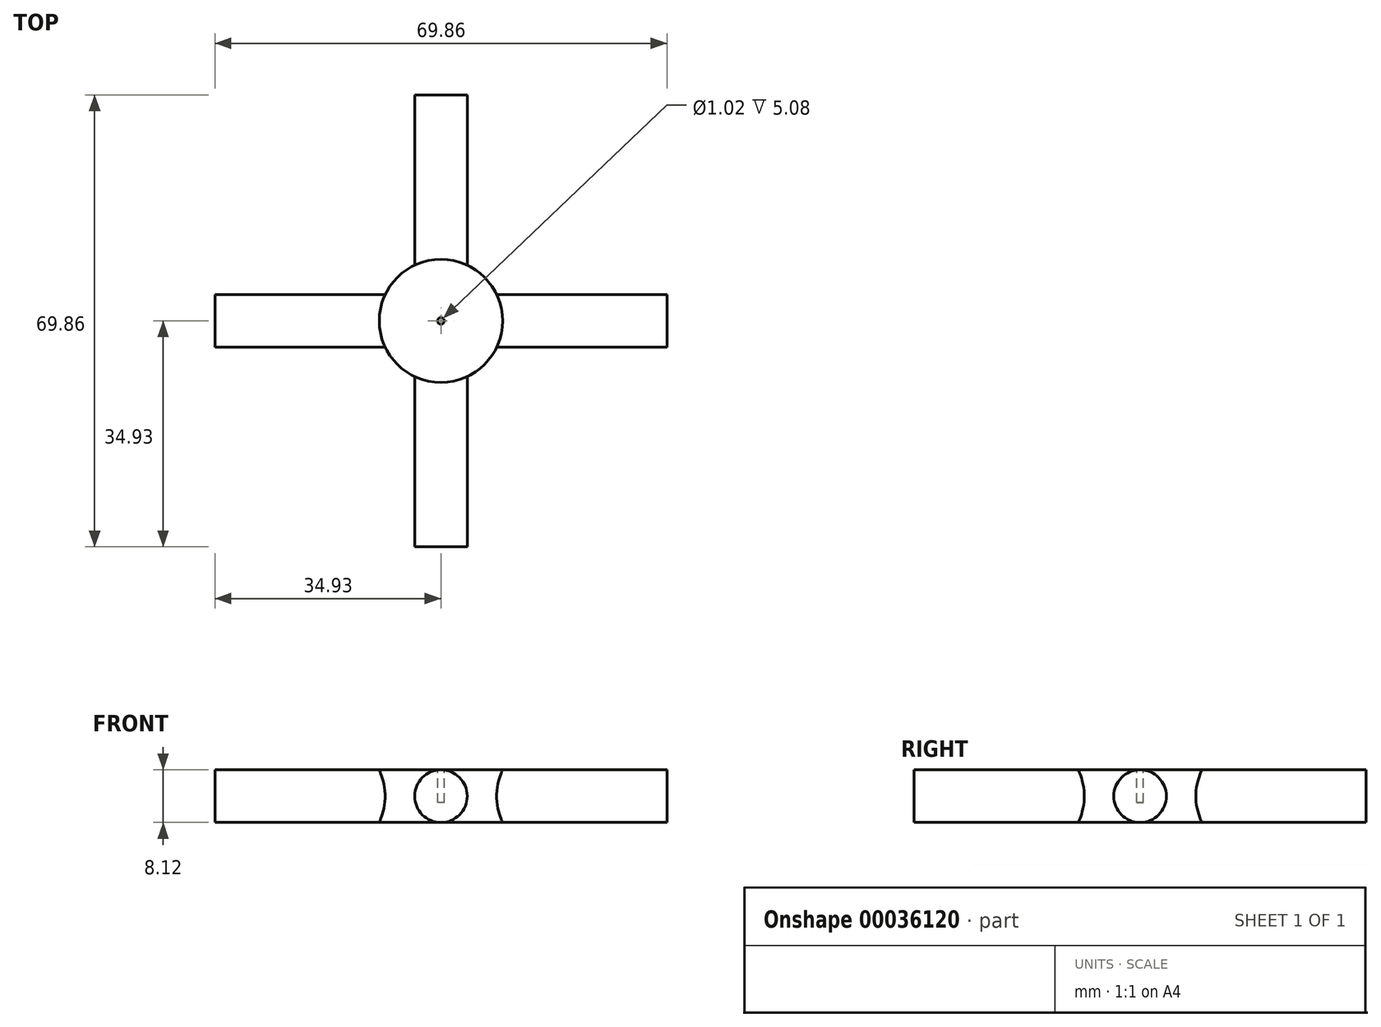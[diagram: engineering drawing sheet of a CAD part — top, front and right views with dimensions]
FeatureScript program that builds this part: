
annotation { "Feature Type Name" : "Feature", "Feature Type Description" : "" }
export const myFeature = defineFeature(function(context is Context, id is Id, definition is map)
    precondition{}
    {
        {
            var Q0;
            Q0=qCreatedBy(makeId("Top.planeOp"),FACE);
            var sketch = newSketch(context, id + "F0", { "sketchPlane" : qUnion([Q0])});
            skCircle(sketch, "E0", {"center": v(0, 0) * mm, "radius": 9.53 * mm});
            skSolve(sketch);
        }
        {
            var Q0;
            Q0 = qSketchRegion(id + "F0", true);
            extrude(context, id + "F1", {"entities" : qUnion([Q0]), "endBound" : BoundingType.SYMMETRIC, "depth" : 8.13 * mm});
        }
        {
            var Q0;
            Q0=qCreatedBy(makeId("Right.planeOp"),FACE);
            var sketch = newSketch(context, id + "F2", { "sketchPlane" : qUnion([Q0])});
            skCircle(sketch, "E1", {"center": v(0, 0) * mm, "radius": 4.06 * mm});
            skSolve(sketch);
        }
        {
            var Q0;
            Q0 = qSketchRegion(id + "F2", true);
            extrude(context, id + "F3", {"entities" : qUnion([Q0]), "operationType" : NewBodyOperationType.ADD, "endBound" : BoundingType.SYMMETRIC, "depth" : 69.85 * mm});
        }
        {
            var Q0;
            Q0=qCreatedBy(makeId("Front.planeOp"),FACE);
            var sketch = newSketch(context, id + "F4", { "sketchPlane" : qUnion([Q0])});
            skCircle(sketch, "E2", {"center": v(0, 0) * mm, "radius": 4.06 * mm});
            skSolve(sketch);
        }
        {
            var Q0;
            Q0 = qSketchRegion(id + "F4", true);
            extrude(context, id + "F5", {"entities" : qUnion([Q0]), "operationType" : NewBodyOperationType.ADD, "endBound" : BoundingType.SYMMETRIC, "depth" : 69.85 * mm});
        }
        {
            var Q0;
            Q0=makeQuery(id+"F1.opExtrude","CAP_FACE",FACE,{"disambiguationData":[OSD([sQuery(id+"F0.wireOp",EDGE,"E0")])],"isStart":false});
            var sketch = newSketch(context, id + "F6", { "sketchPlane" : qUnion([Q0])});
            skCircle(sketch, "E3", {"center": v(0, 0) * mm, "radius": 0.5 * mm});
            skSolve(sketch);
        }
        {
            var Q0;
            Q0=makeQuery(id+"F6.imprint","IMPRINT",FACE,{"disambiguationData":[TD([[makeQuery(id+"F6.imprint","IMPRINT",EDGE,{"derivedFrom":sQuery(id+"F6.wireOp",EDGE,"E3")}),1.0]])]});
            var Q1;
            Q1=sQuery(id+"F6.wireOp",EDGE,"E3");
            extrude(context, id + "F7", {"entities" : qUnion([Q0]), "operationType" : NewBodyOperationType.REMOVE, "surfaceEntities" : qUnion([Q1]), "oppositeDirection" : true, "depth" : 5.08 * mm});
        }
    });
